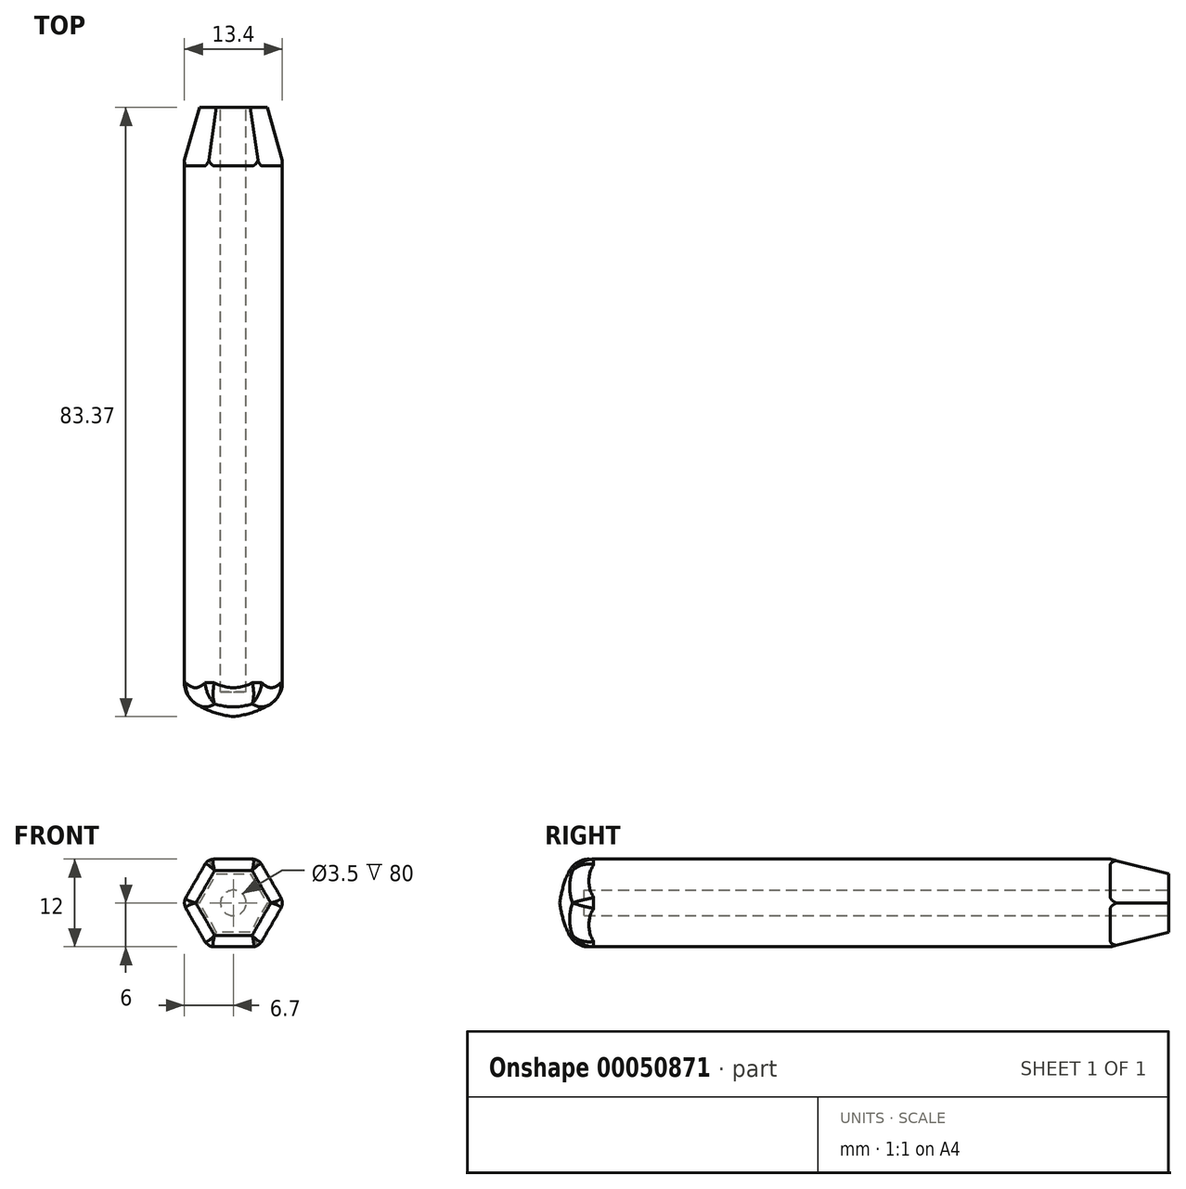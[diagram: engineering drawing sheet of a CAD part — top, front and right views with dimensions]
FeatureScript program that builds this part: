
annotation { "Feature Type Name" : "Feature", "Feature Type Description" : "" }
export const myFeature = defineFeature(function(context is Context, id is Id, definition is map)
    precondition{}
    {
        {
            var Q0;
            Q0=qCreatedBy(makeId("Front.planeOp"),FACE);
            var sketch = newSketch(context, id + "F0", { "sketchPlane" : qUnion([Q0])});
            skCircle(sketch, "E0.cCircle", {"center": v(0, 0) * mm, "radius": 6 * mm, "construction": true});
            skLineSegment(sketch, "E0.0", {"start": v(-6.93, 0) * mm, "end": v(-3.46, 6) * mm});
            skLineSegment(sketch, "E0.1", {"start": v(-3.46, 6) * mm, "end": v(3.46, 6) * mm});
            skLineSegment(sketch, "E0.2", {"start": v(3.46, 6) * mm, "end": v(6.93, 0) * mm});
            skLineSegment(sketch, "E0.3", {"start": v(6.93, 0) * mm, "end": v(3.46, -6) * mm});
            skLineSegment(sketch, "E0.4", {"start": v(3.46, -6) * mm, "end": v(-3.46, -6) * mm});
            skLineSegment(sketch, "E0.5", {"start": v(-3.46, -6) * mm, "end": v(-6.93, 0) * mm});
            skPoint(sketch, "E0.0.midPoint", {"position": v(-5.2, 3) * mm});
            skCircle(sketch, "E1", {"center": v(0, 0) * mm, "radius": 1.75 * mm});
            skSolve(sketch);
        }
        {
            var Q0;
            Q0=makeQuery(id+"F0.imprint","IMPRINT",FACE,{"disambiguationData":[TD([[makeQuery(id+"F0.imprint","IMPRINT",EDGE,{"derivedFrom":sQuery(id+"F0.wireOp",EDGE,"E0.0")}),-1.0]])]});
            extrude(context, id + "F1", {"entities" : qUnion([Q0]), "depth" : 80 * mm});
        }
        {
            var Q0;
            Q0=makeQuery(id+"F1.opExtrude","CAP_EDGE",EDGE,{"disambiguationData":[OSD([sQuery(id+"F0.wireOp",EDGE,"E0.0")])],"isStart":true});
            var Q1;
            Q1=makeQuery(id+"F1.opExtrude","CAP_EDGE",EDGE,{"disambiguationData":[OSD([sQuery(id+"F0.wireOp",EDGE,"E0.5")])],"isStart":true});
            var Q2;
            Q2=makeQuery(id+"F1.opExtrude","CAP_EDGE",EDGE,{"disambiguationData":[OSD([sQuery(id+"F0.wireOp",EDGE,"E0.3")])],"isStart":true});
            var Q3;
            Q3=makeQuery(id+"F1.opExtrude","CAP_EDGE",EDGE,{"disambiguationData":[OSD([sQuery(id+"F0.wireOp",EDGE,"E0.1")])],"isStart":true});
            var Q4;
            Q4=makeQuery(id+"F1.opExtrude","CAP_EDGE",EDGE,{"disambiguationData":[OSD([sQuery(id+"F0.wireOp",EDGE,"E0.2")])],"isStart":true});
            var Q5;
            Q5=makeQuery(id+"F1.opExtrude","CAP_EDGE",EDGE,{"disambiguationData":[OSD([sQuery(id+"F0.wireOp",EDGE,"E0.4")])],"isStart":true});
            chamfer(context, id + "F2", {"entities" : qUnion([Q0, Q1, Q2, Q3, Q4, Q5]), "chamferType" : ChamferType.TWO_OFFSETS, "width1" : 2 * mm, "oppositeDirection" : false, "width2" : 8 * mm, "tangentPropagation" : true});
        }
        {
            var Q0;
            Q0=qCreatedBy(makeId("Top.planeOp"),FACE);
            var sketch = newSketch(context, id + "F3", { "sketchPlane" : qUnion([Q0])});
            skFitSpline(sketch, "E2", {"points": [v(0, -83.37) * mm, v(-6.93, -80) * mm], "startDerivative": vector(-9.1, 1.31) * mm, "endDerivative": vector(-5.08, 5.94) * mm});
            skLineSegment(sketch, "E3", {"start": v(-6.93, -80) * mm, "end": v(0, -80) * mm});
            skLineSegment(sketch, "E4", {"start": v(0, -80) * mm, "end": v(0, -83.37) * mm});
            skSolve(sketch);
        }
        {
            var Q0;
            Q0=makeQuery(id+"F3.imprint","IMPRINT",FACE,{"disambiguationData":[TD([[makeQuery(id+"F3.imprint","IMPRINT",EDGE,{"derivedFrom":sQuery(id+"F3.wireOp",EDGE,"E2")}),-1.0]])]});
            var Q1;
            Q1=sQuery(id+"F3.wireOp",EDGE,"E4");
            revolve(context, id + "F4", {"operationType" : NewBodyOperationType.ADD, "entities" : qUnion([Q0]), "axis" : qUnion([Q1]), "revolveType" : RevolveType.FULL});
        }
        {
            var Q0;
            {var subQ0=sQuery(id+"F3.wireOp",EDGE,"E2");var subQ1=sQuery(id+"F3.wireOp",EDGE,"E3");Q0=makeQuery(id+"F4.boolean.opBoolean","SPLIT",EDGE,{"disambiguationData":[TD([makeQuery(id+"F1.opExtrude","SWEPT_FACE",FACE,{"disambiguationData":[OSD([sQuery(id+"F0.wireOp",EDGE,"E0.3")])]}),makeQuery(id+"F1.opExtrude","SWEPT_FACE",FACE,{"disambiguationData":[OSD([sQuery(id+"F0.wireOp",EDGE,"E0.4")])]}),makeQuery(id+"F1.opExtrude","SWEPT_FACE",FACE,{"disambiguationData":[OSD([sQuery(id+"F0.wireOp",EDGE,"E0.5")])]}),makeQuery(id+"F4.opRevolve","SWEPT_FACE",FACE,{"disambiguationData":[OSD([subQ0])]}),makeQuery(id+"F4.opRevolve","SWEPT_FACE",FACE,{"disambiguationData":[OSD([subQ1])]})])],"derivedFrom":makeQuery(id+"F4.opRevolve","SWEPT_EDGE",EDGE,{"disambiguationData":[OSD([subQ0,subQ1])]})});}
            var Q1;
            {var subQ0=sQuery(id+"F3.wireOp",EDGE,"E2");var subQ1=sQuery(id+"F3.wireOp",EDGE,"E3");Q1=makeQuery(id+"F4.boolean.opBoolean","SPLIT",EDGE,{"disambiguationData":[TD([makeQuery(id+"F1.opExtrude","SWEPT_FACE",FACE,{"disambiguationData":[OSD([sQuery(id+"F0.wireOp",EDGE,"E0.0")])]}),makeQuery(id+"F1.opExtrude","SWEPT_FACE",FACE,{"disambiguationData":[OSD([sQuery(id+"F0.wireOp",EDGE,"E0.4")])]}),makeQuery(id+"F1.opExtrude","SWEPT_FACE",FACE,{"disambiguationData":[OSD([sQuery(id+"F0.wireOp",EDGE,"E0.5")])]}),makeQuery(id+"F4.opRevolve","SWEPT_FACE",FACE,{"disambiguationData":[OSD([subQ0])]}),makeQuery(id+"F4.opRevolve","SWEPT_FACE",FACE,{"disambiguationData":[OSD([subQ1])]})])],"derivedFrom":makeQuery(id+"F4.opRevolve","SWEPT_EDGE",EDGE,{"disambiguationData":[OSD([subQ0,subQ1])]})});}
            var Q2;
            {var subQ0=sQuery(id+"F3.wireOp",EDGE,"E2");var subQ1=sQuery(id+"F3.wireOp",EDGE,"E3");Q2=makeQuery(id+"F4.boolean.opBoolean","SPLIT",EDGE,{"disambiguationData":[TD([makeQuery(id+"F1.opExtrude","SWEPT_FACE",FACE,{"disambiguationData":[OSD([sQuery(id+"F0.wireOp",EDGE,"E0.2")])]}),makeQuery(id+"F1.opExtrude","SWEPT_FACE",FACE,{"disambiguationData":[OSD([sQuery(id+"F0.wireOp",EDGE,"E0.3")])]}),makeQuery(id+"F1.opExtrude","SWEPT_FACE",FACE,{"disambiguationData":[OSD([sQuery(id+"F0.wireOp",EDGE,"E0.4")])]}),makeQuery(id+"F4.opRevolve","SWEPT_FACE",FACE,{"disambiguationData":[OSD([subQ0])]}),makeQuery(id+"F4.opRevolve","SWEPT_FACE",FACE,{"disambiguationData":[OSD([subQ1])]})])],"derivedFrom":makeQuery(id+"F4.opRevolve","SWEPT_EDGE",EDGE,{"disambiguationData":[OSD([subQ0,subQ1])]})});}
            var Q3;
            {var subQ0=sQuery(id+"F3.wireOp",EDGE,"E2");var subQ1=sQuery(id+"F3.wireOp",EDGE,"E3");Q3=makeQuery(id+"F4.boolean.opBoolean","SPLIT",EDGE,{"disambiguationData":[TD([makeQuery(id+"F1.opExtrude","SWEPT_FACE",FACE,{"disambiguationData":[OSD([sQuery(id+"F0.wireOp",EDGE,"E0.0")])]}),makeQuery(id+"F1.opExtrude","SWEPT_FACE",FACE,{"disambiguationData":[OSD([sQuery(id+"F0.wireOp",EDGE,"E0.1")])]}),makeQuery(id+"F1.opExtrude","SWEPT_FACE",FACE,{"disambiguationData":[OSD([sQuery(id+"F0.wireOp",EDGE,"E0.5")])]}),makeQuery(id+"F4.opRevolve","SWEPT_FACE",FACE,{"disambiguationData":[OSD([subQ0])]}),makeQuery(id+"F4.opRevolve","SWEPT_FACE",FACE,{"disambiguationData":[OSD([subQ1])]})])],"derivedFrom":makeQuery(id+"F4.opRevolve","SWEPT_EDGE",EDGE,{"disambiguationData":[OSD([subQ0,subQ1])]})});}
            var Q4;
            {var subQ0=sQuery(id+"F3.wireOp",EDGE,"E2");var subQ1=sQuery(id+"F3.wireOp",EDGE,"E3");Q4=makeQuery(id+"F4.boolean.opBoolean","SPLIT",EDGE,{"disambiguationData":[TD([makeQuery(id+"F1.opExtrude","SWEPT_FACE",FACE,{"disambiguationData":[OSD([sQuery(id+"F0.wireOp",EDGE,"E0.0")])]}),makeQuery(id+"F1.opExtrude","SWEPT_FACE",FACE,{"disambiguationData":[OSD([sQuery(id+"F0.wireOp",EDGE,"E0.1")])]}),makeQuery(id+"F1.opExtrude","SWEPT_FACE",FACE,{"disambiguationData":[OSD([sQuery(id+"F0.wireOp",EDGE,"E0.2")])]}),makeQuery(id+"F4.opRevolve","SWEPT_FACE",FACE,{"disambiguationData":[OSD([subQ0])]}),makeQuery(id+"F4.opRevolve","SWEPT_FACE",FACE,{"disambiguationData":[OSD([subQ1])]})])],"derivedFrom":makeQuery(id+"F4.opRevolve","SWEPT_EDGE",EDGE,{"disambiguationData":[OSD([subQ0,subQ1])]})});}
            var Q5;
            {var subQ0=sQuery(id+"F3.wireOp",EDGE,"E2");var subQ1=sQuery(id+"F3.wireOp",EDGE,"E3");Q5=makeQuery(id+"F4.boolean.opBoolean","SPLIT",EDGE,{"disambiguationData":[TD([makeQuery(id+"F1.opExtrude","SWEPT_FACE",FACE,{"disambiguationData":[OSD([sQuery(id+"F0.wireOp",EDGE,"E0.1")])]}),makeQuery(id+"F1.opExtrude","SWEPT_FACE",FACE,{"disambiguationData":[OSD([sQuery(id+"F0.wireOp",EDGE,"E0.2")])]}),makeQuery(id+"F1.opExtrude","SWEPT_FACE",FACE,{"disambiguationData":[OSD([sQuery(id+"F0.wireOp",EDGE,"E0.3")])]}),makeQuery(id+"F4.opRevolve","SWEPT_FACE",FACE,{"disambiguationData":[OSD([subQ0])]}),makeQuery(id+"F4.opRevolve","SWEPT_FACE",FACE,{"disambiguationData":[OSD([subQ1])]})])],"derivedFrom":makeQuery(id+"F4.opRevolve","SWEPT_EDGE",EDGE,{"disambiguationData":[OSD([subQ0,subQ1])]})});}
            fillet(context, id + "F5", {"entities" : qUnion([Q0, Q1, Q2, Q3, Q4, Q5]), "radius" : 3 * mm, "tangentPropagation" : true, "allowEdgeOverflow" : false});
        }
        {
            var Q0;
            Q0=makeQuery(id+"F1.opExtrude","SWEPT_EDGE",EDGE,{"disambiguationData":[OSD([sQuery(id+"F0.wireOp",EDGE,"E0.1"),sQuery(id+"F0.wireOp",EDGE,"E0.2")])]});
            var Q1;
            Q1=makeQuery(id+"F1.opExtrude","SWEPT_EDGE",EDGE,{"disambiguationData":[OSD([sQuery(id+"F0.wireOp",EDGE,"E0.0"),sQuery(id+"F0.wireOp",EDGE,"E0.1")])]});
            var Q2;
            Q2=makeQuery(id+"F1.opExtrude","SWEPT_EDGE",EDGE,{"disambiguationData":[OSD([sQuery(id+"F0.wireOp",EDGE,"E0.2"),sQuery(id+"F0.wireOp",EDGE,"E0.3")])]});
            var Q3;
            Q3=makeQuery(id+"F1.opExtrude","SWEPT_EDGE",EDGE,{"disambiguationData":[OSD([sQuery(id+"F0.wireOp",EDGE,"E0.3"),sQuery(id+"F0.wireOp",EDGE,"E0.4")])]});
            var Q4;
            Q4=makeQuery(id+"F1.opExtrude","SWEPT_EDGE",EDGE,{"disambiguationData":[OSD([sQuery(id+"F0.wireOp",EDGE,"E0.4"),sQuery(id+"F0.wireOp",EDGE,"E0.5")])]});
            var Q5;
            Q5=makeQuery(id+"F1.opExtrude","SWEPT_EDGE",EDGE,{"disambiguationData":[OSD([sQuery(id+"F0.wireOp",EDGE,"E0.0"),sQuery(id+"F0.wireOp",EDGE,"E0.5")])]});
            fillet(context, id + "F6", {"entities" : qUnion([Q0, Q1, Q2, Q3, Q4, Q5]), "radius" : 1.5 * mm, "tangentPropagation" : true, "allowEdgeOverflow" : false});
        }
    });
